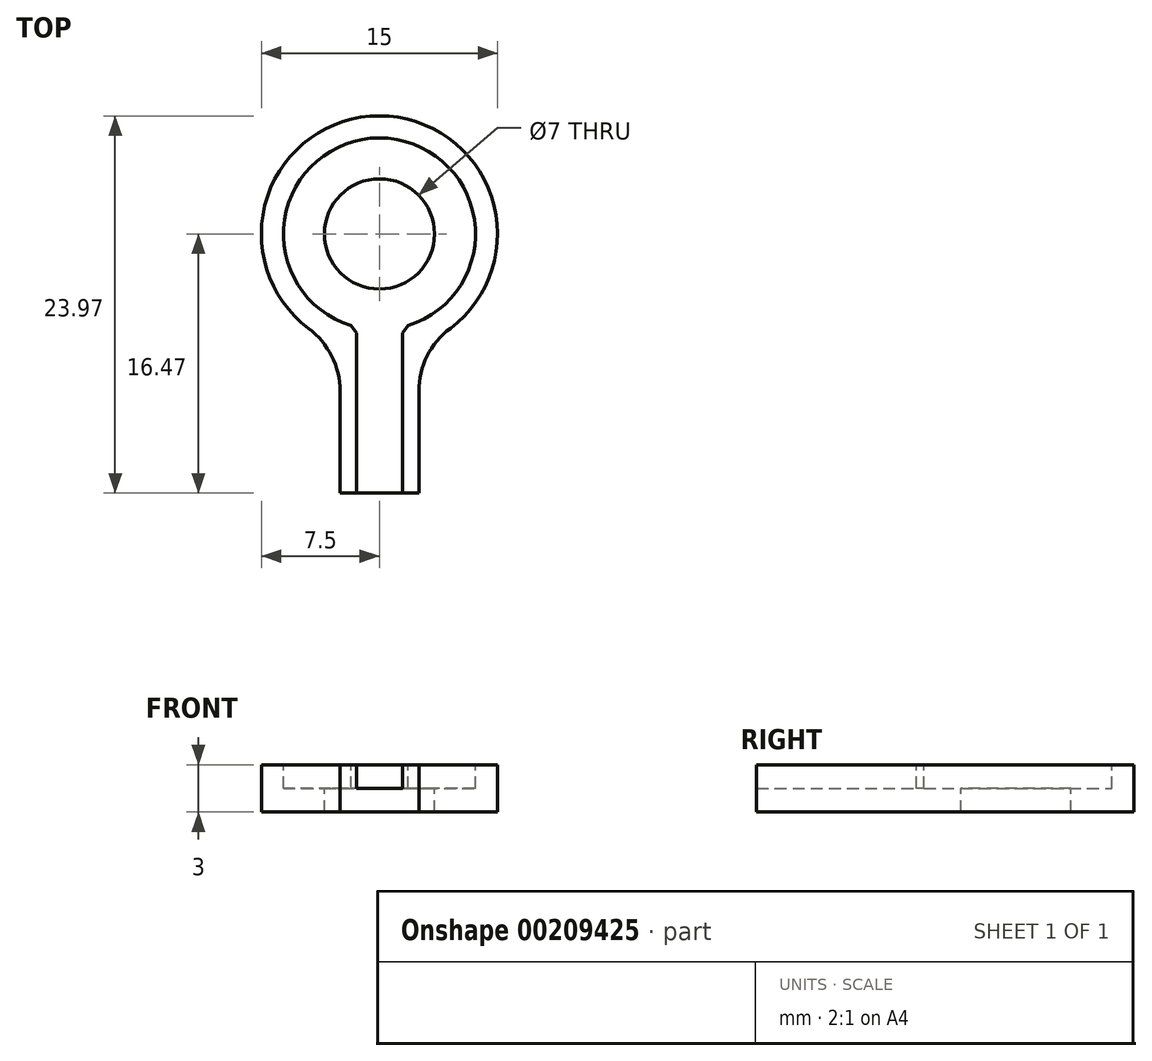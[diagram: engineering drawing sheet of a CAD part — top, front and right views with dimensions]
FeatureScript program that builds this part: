
annotation { "Feature Type Name" : "Feature", "Feature Type Description" : "" }
export const myFeature = defineFeature(function(context is Context, id is Id, definition is map)
    precondition{}
    {
        {
            var Q0;
            Q0=qCreatedBy(makeId("Top.planeOp"),FACE);
            var sketch = newSketch(context, id + "F0", { "sketchPlane" : qUnion([Q0])});
            skCircle(sketch, "E0", {"center": v(0, 0) * mm, "radius": 7.5 * mm});
            skLineSegment(sketch, "E1.bottom", {"start": v(-2.5, -7.07) * mm, "end": v(2.5, -7.07) * mm});
            skLineSegment(sketch, "E1.top", {"start": v(-2.5, -16.47) * mm, "end": v(2.5, -16.47) * mm});
            skLineSegment(sketch, "E1.left", {"start": v(-2.5, -7.07) * mm, "end": v(-2.5, -16.47) * mm});
            skLineSegment(sketch, "E1.right", {"start": v(2.5, -7.07) * mm, "end": v(2.5, -16.47) * mm});
            skPoint(sketch, "E2", {"position": v(0, -16.47) * mm});
            skSolve(sketch);
        }
        {
            var Q0;
            Q0 = qSketchRegion(id + "F0", true);
            extrude(context, id + "F1", {"entities" : qUnion([Q0]), "depth" : 3 * mm});
        }
        {
            var Q0;
            Q0=makeQuery(id+"F1.opExtrude","CAP_FACE",FACE,{"disambiguationData":[OSD([sQuery(id+"F0.wireOp",EDGE,"E0"),sQuery(id+"F0.wireOp",EDGE,"E1.top"),sQuery(id+"F0.wireOp",EDGE,"E1.left"),sQuery(id+"F0.wireOp",EDGE,"E1.right")])],"isStart":false});
            var sketch = newSketch(context, id + "F2", { "sketchPlane" : qUnion([Q0])});
            skCircle(sketch, "E3", {"center": v(0, 0) * mm, "radius": 6.1 * mm});
            skLineSegment(sketch, "E4.bottom", {"start": v(-1.45, -16.47) * mm, "end": v(1.45, -16.47) * mm});
            skLineSegment(sketch, "E4.top", {"start": v(-1.45, -5.93) * mm, "end": v(1.45, -5.93) * mm});
            skLineSegment(sketch, "E4.left", {"start": v(-1.45, -16.47) * mm, "end": v(-1.45, -5.93) * mm});
            skLineSegment(sketch, "E4.right", {"start": v(1.45, -16.47) * mm, "end": v(1.45, -5.93) * mm});
            skPoint(sketch, "E5", {"position": v(0, -16.47) * mm});
            skSolve(sketch);
        }
        {
            var Q0;
            Q0 = qSketchRegion(id + "F2", true);
            extrude(context, id + "F3", {"entities" : qUnion([Q0]), "operationType" : NewBodyOperationType.REMOVE, "oppositeDirection" : true, "depth" : 1.5 * mm});
        }
        {
            var Q0;
            Q0=makeQuery(id+"F3.boolean.opBoolean","COPY",FACE,{"derivedFrom":makeQuery(id+"F3.opExtrude","CAP_FACE",FACE,{"disambiguationData":[OSD([sQuery(id+"F2.wireOp",EDGE,"E3"),sQuery(id+"F2.wireOp",EDGE,"E4.bottom"),sQuery(id+"F2.wireOp",EDGE,"E4.left"),sQuery(id+"F2.wireOp",EDGE,"E4.right")])],"isStart":false})});
            var sketch = newSketch(context, id + "F4", { "sketchPlane" : qUnion([Q0])});
            skCircle(sketch, "E6", {"center": v(0, 0) * mm, "radius": 3.5 * mm});
            skSolve(sketch);
        }
        {
            var Q0;
            Q0 = qSketchRegion(id + "F4", true);
            extrude(context, id + "F5", {"entities" : qUnion([Q0]), "operationType" : NewBodyOperationType.REMOVE, "endBound" : BoundingType.UP_TO_NEXT, "oppositeDirection" : true, "depth" : 25 * mm});
        }
        {
            var Q0;
            Q0=makeQuery(id+"F3.boolean.opBoolean","COPY",EDGE,{"derivedFrom":makeQuery(id+"F3.opExtrude","SWEPT_EDGE",EDGE,{"disambiguationData":[OSD([sQuery(id+"F2.wireOp",EDGE,"E3"),sQuery(id+"F2.wireOp",EDGE,"E4.top"),sQuery(id+"F2.wireOp",EDGE,"E4.right")])]})});
            var Q1;
            Q1=makeQuery(id+"F3.boolean.opBoolean","COPY",EDGE,{"derivedFrom":makeQuery(id+"F3.opExtrude","SWEPT_EDGE",EDGE,{"disambiguationData":[OSD([sQuery(id+"F2.wireOp",EDGE,"E3"),sQuery(id+"F2.wireOp",EDGE,"E4.top"),sQuery(id+"F2.wireOp",EDGE,"E4.left")])]})});
            chamfer(context, id + "F6", {"entities" : qUnion([Q0, Q1]), "width" : 0.5 * mm, "tangentPropagation" : true});
        }
        {
            var Q0;
            Q0=makeQuery(id+"F1.opExtrude","SWEPT_EDGE",EDGE,{"disambiguationData":[OSD([sQuery(id+"F0.wireOp",EDGE,"E0"),sQuery(id+"F0.wireOp",EDGE,"E1.bottom"),sQuery(id+"F0.wireOp",EDGE,"E1.left")])]});
            var Q1;
            Q1=makeQuery(id+"F1.opExtrude","SWEPT_EDGE",EDGE,{"disambiguationData":[OSD([sQuery(id+"F0.wireOp",EDGE,"E0"),sQuery(id+"F0.wireOp",EDGE,"E1.bottom"),sQuery(id+"F0.wireOp",EDGE,"E1.right")])]});
            fillet(context, id + "F7", {"entities" : qUnion([Q0, Q1]), "radius" : 5 * mm, "tangentPropagation" : true, "allowEdgeOverflow" : false});
        }
    });
